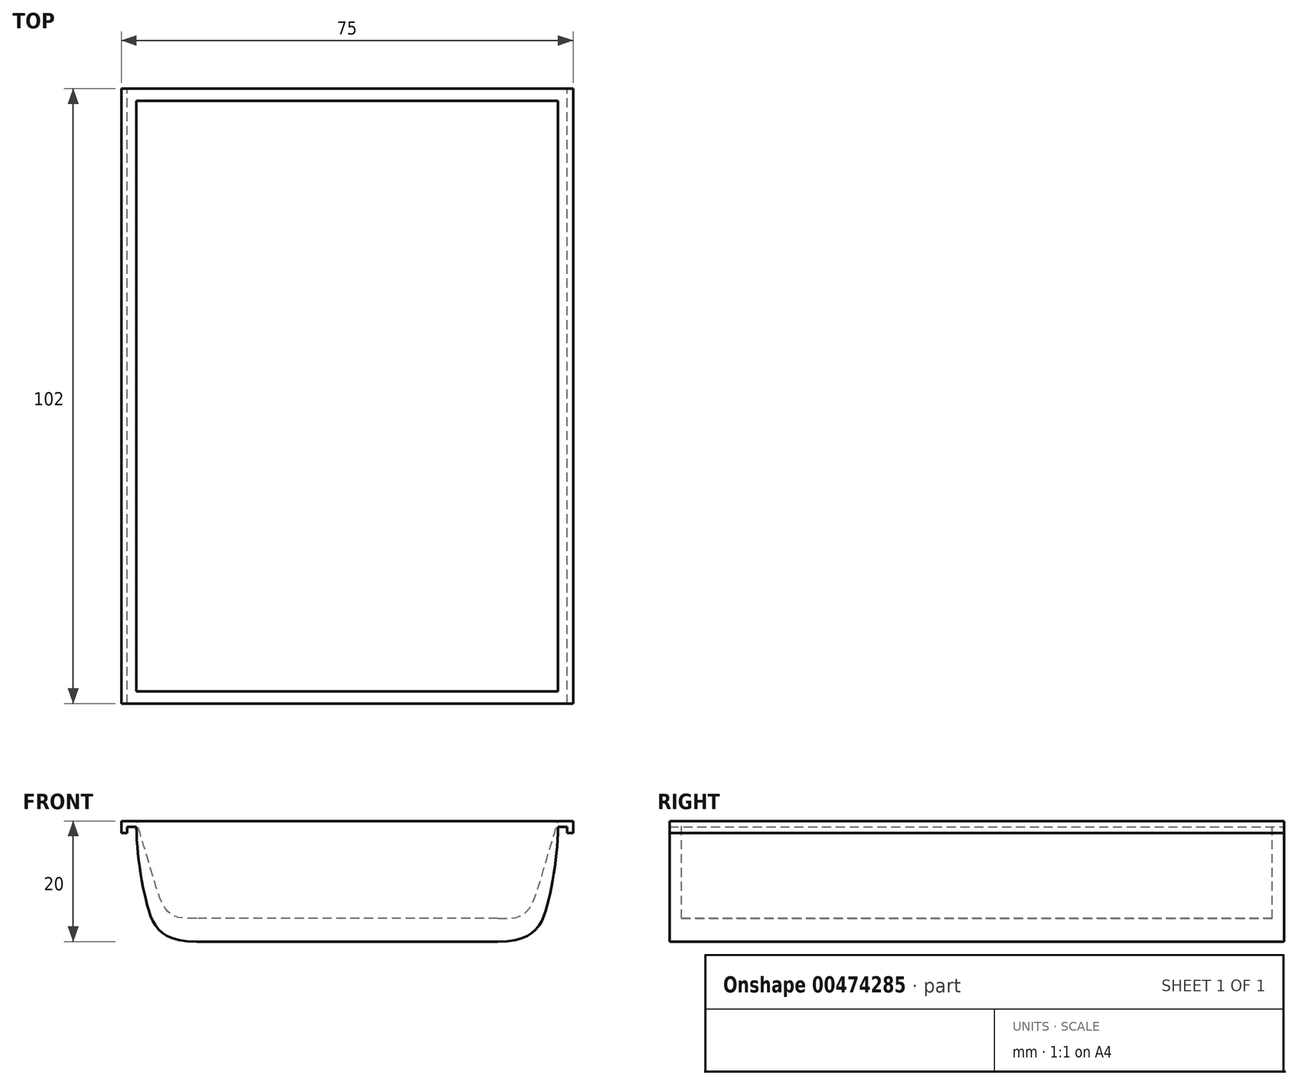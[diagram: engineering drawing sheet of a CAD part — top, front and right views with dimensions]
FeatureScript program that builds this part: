
annotation { "Feature Type Name" : "Feature", "Feature Type Description" : "" }
export const myFeature = defineFeature(function(context is Context, id is Id, definition is map)
    precondition{}
    {
        {
            var Q0;
            Q0=qCreatedBy(makeId("Front.planeOp"),FACE);
            var sketch = newSketch(context, id + "F0", { "sketchPlane" : qUnion([Q0])});
            skLineSegment(sketch, "E0", {"start": v(-25, 0) * mm, "end": v(0, 0) * mm});
            skFitSpline(sketch, "E1", {"points": [v(-25, 0) * mm, v(-33.2, 6.07) * mm, v(-35, 20) * mm], "startDerivative": vector(-39.49, 0) * mm, "endDerivative": vector(0.33, 24.4) * mm});
            skLineSegment(sketch, "E2.MirrorCS", {"start": v(25, 0) * mm, "end": v(0, 0) * mm});
            skFitSpline(sketch, "E3.MirrorCS", {"points": [v(25, 0) * mm, v(33.2, 6.07) * mm, v(35, 20) * mm], "startDerivative": vector(39.49, 0) * mm, "endDerivative": vector(-0.33, 24.4) * mm});
            skLineSegment(sketch, "E4", {"start": v(-25, 3.83) * mm, "end": v(0, 3.83) * mm});
            skLineSegment(sketch, "E5.MirrorCS", {"start": v(25, 3.83) * mm, "end": v(0, 3.83) * mm});
            skLineSegment(sketch, "E6", {"start": v(-35, 20) * mm, "end": v(-37.5, 20) * mm});
            skLineSegment(sketch, "E7", {"start": v(-37.5, 20) * mm, "end": v(-37.5, 19) * mm});
            skLineSegment(sketch, "E8", {"start": v(-37.5, 19) * mm, "end": v(-35, 19) * mm});
            skLineSegment(sketch, "E9.MirrorCS", {"start": v(35, 20) * mm, "end": v(37.5, 20) * mm});
            skLineSegment(sketch, "E10.MirrorCS", {"start": v(37.5, 19) * mm, "end": v(35, 19) * mm});
            skLineSegment(sketch, "E11", {"start": v(37.5, 20) * mm, "end": v(37.5, 19) * mm});
            skLineSegment(sketch, "E12", {"start": v(-37.5, 19) * mm, "end": v(-37.5, 18) * mm});
            skLineSegment(sketch, "E13", {"start": v(-37.5, 18) * mm, "end": v(-36.5, 18) * mm});
            skLineSegment(sketch, "E14", {"start": v(-36.5, 18) * mm, "end": v(-36.5, 19) * mm});
            skLineSegment(sketch, "E15.MirrorCS", {"start": v(37.5, 19) * mm, "end": v(37.5, 18) * mm});
            skLineSegment(sketch, "E16.MirrorCS", {"start": v(37.5, 18) * mm, "end": v(36.5, 18) * mm});
            skLineSegment(sketch, "E17.MirrorCS", {"start": v(36.5, 18) * mm, "end": v(36.5, 19) * mm});
            skLineSegment(sketch, "E18", {"start": v(35, 20) * mm, "end": v(-35, 20) * mm});
            skFitSpline(sketch, "E19", {"points": [v(25, 3.83) * mm, v(29.36, 4.6) * mm, v(32.24, 10.76) * mm, v(35, 20) * mm], "startDerivative": vector(17.91, 0) * mm, "endDerivative": vector(7.06, 23.4) * mm});
            skFitSpline(sketch, "E20.MirrorCS", {"points": [v(-25, 3.83) * mm, v(-29.36, 4.6) * mm, v(-32.24, 10.76) * mm, v(-35, 20) * mm], "startDerivative": vector(-17.91, 0) * mm, "endDerivative": vector(-7.06, 23.4) * mm});
            skSolve(sketch);
        }
        {
            var Q0;
            Q0=makeQuery(id+"F0.imprint","IMPRINT",FACE,{"disambiguationData":[TD([[makeQuery(id+"F0.imprint","IMPRINT",EDGE,{"derivedFrom":sQuery(id+"F0.wireOp",EDGE,"E0")}),1.0]])]});
            var Q1;
            {var subQ0=sQuery(id+"F0.wireOp",EDGE,"E6");Q1=makeQuery(id+"F0.imprint","IMPRINT",FACE,{"disambiguationData":[TD([[makeQuery(id+"F0.imprint","IMPRINT",EDGE,{"derivedFrom":subQ0}),1.0]])]});}
            var Q2;
            {var subQ0=sQuery(id+"F0.wireOp",EDGE,"E9.MirrorCS");Q2=makeQuery(id+"F0.imprint","IMPRINT",FACE,{"disambiguationData":[TD([[makeQuery(id+"F0.imprint","IMPRINT",EDGE,{"derivedFrom":subQ0}),-1.0]])]});}
            var Q3;
            {var subQ0=sQuery(id+"F0.wireOp",EDGE,"E12");Q3=makeQuery(id+"F0.imprint","IMPRINT",FACE,{"disambiguationData":[TD([[makeQuery(id+"F0.imprint","IMPRINT",EDGE,{"derivedFrom":subQ0}),1.0]])]});}
            var Q4;
            {var subQ0=sQuery(id+"F0.wireOp",EDGE,"E15.MirrorCS");Q4=makeQuery(id+"F0.imprint","IMPRINT",FACE,{"disambiguationData":[TD([[makeQuery(id+"F0.imprint","IMPRINT",EDGE,{"derivedFrom":subQ0}),-1.0]])]});}
            extrude(context, id + "F1", {"entities" : qUnion([Q0, Q1, Q2, Q3, Q4]), "depth" : 100 * mm});
        }
        {
            var Q0;
            Q0=makeQuery(id+"F1.opExtrude","CAP_FACE",FACE,{"disambiguationData":[OSD([sQuery(id+"F0.wireOp",EDGE,"E0"),sQuery(id+"F0.wireOp",EDGE,"E1"),sQuery(id+"F0.wireOp",EDGE,"E2.MirrorCS"),sQuery(id+"F0.wireOp",EDGE,"E3.MirrorCS"),sQuery(id+"F0.wireOp",EDGE,"E4"),sQuery(id+"F0.wireOp",EDGE,"E5.MirrorCS"),sQuery(id+"F0.wireOp",EDGE,"E6"),sQuery(id+"F0.wireOp",EDGE,"E7"),sQuery(id+"F0.wireOp",EDGE,"E8"),sQuery(id+"F0.wireOp",EDGE,"E9.MirrorCS"),sQuery(id+"F0.wireOp",EDGE,"E10.MirrorCS"),sQuery(id+"F0.wireOp",EDGE,"E11"),sQuery(id+"F0.wireOp",EDGE,"E12"),sQuery(id+"F0.wireOp",EDGE,"E13"),sQuery(id+"F0.wireOp",EDGE,"E14"),sQuery(id+"F0.wireOp",EDGE,"E15.MirrorCS"),sQuery(id+"F0.wireOp",EDGE,"E16.MirrorCS"),sQuery(id+"F0.wireOp",EDGE,"E17.MirrorCS"),sQuery(id+"F0.wireOp",EDGE,"E19"),sQuery(id+"F0.wireOp",EDGE,"E20.MirrorCS")])],"isStart":false});
            var sketch = newSketch(context, id + "F2", { "sketchPlane" : qUnion([Q0])});
            skLineSegment(sketch, "E21", {"start": v(-35, 20) * mm, "end": v(35, 20) * mm});
            skSolve(sketch);
        }
        {
            var Q0;
            Q0=makeQuery(id+"F1.opExtrude","CAP_FACE",FACE,{"disambiguationData":[OSD([sQuery(id+"F0.wireOp",EDGE,"E0"),sQuery(id+"F0.wireOp",EDGE,"E1"),sQuery(id+"F0.wireOp",EDGE,"E2.MirrorCS"),sQuery(id+"F0.wireOp",EDGE,"E3.MirrorCS"),sQuery(id+"F0.wireOp",EDGE,"E4"),sQuery(id+"F0.wireOp",EDGE,"E5.MirrorCS"),sQuery(id+"F0.wireOp",EDGE,"E6"),sQuery(id+"F0.wireOp",EDGE,"E7"),sQuery(id+"F0.wireOp",EDGE,"E8"),sQuery(id+"F0.wireOp",EDGE,"E9.MirrorCS"),sQuery(id+"F0.wireOp",EDGE,"E10.MirrorCS"),sQuery(id+"F0.wireOp",EDGE,"E11"),sQuery(id+"F0.wireOp",EDGE,"E12"),sQuery(id+"F0.wireOp",EDGE,"E13"),sQuery(id+"F0.wireOp",EDGE,"E14"),sQuery(id+"F0.wireOp",EDGE,"E15.MirrorCS"),sQuery(id+"F0.wireOp",EDGE,"E16.MirrorCS"),sQuery(id+"F0.wireOp",EDGE,"E17.MirrorCS"),sQuery(id+"F0.wireOp",EDGE,"E19"),sQuery(id+"F0.wireOp",EDGE,"E20.MirrorCS")])],"isStart":false});
            var Q1;
            Q1 = qSketchRegion(id + "F0", true);
            var Q2;
            Q2=makeQuery(id+"F2.imprint","IMPRINT",FACE,{"disambiguationData":[TD([[makeQuery(id+"F2.imprint","IMPRINT",EDGE,{"derivedFrom":sQuery(id+"F2.wireOp",EDGE,"E21")}),-1.0]])]});
            extrude(context, id + "F3", {"entities" : qUnion([Q0, Q1, Q2]), "operationType" : NewBodyOperationType.ADD, "endBound" : BoundingType.SYMMETRIC, "depth" : 2 * mm});
        }
    });
